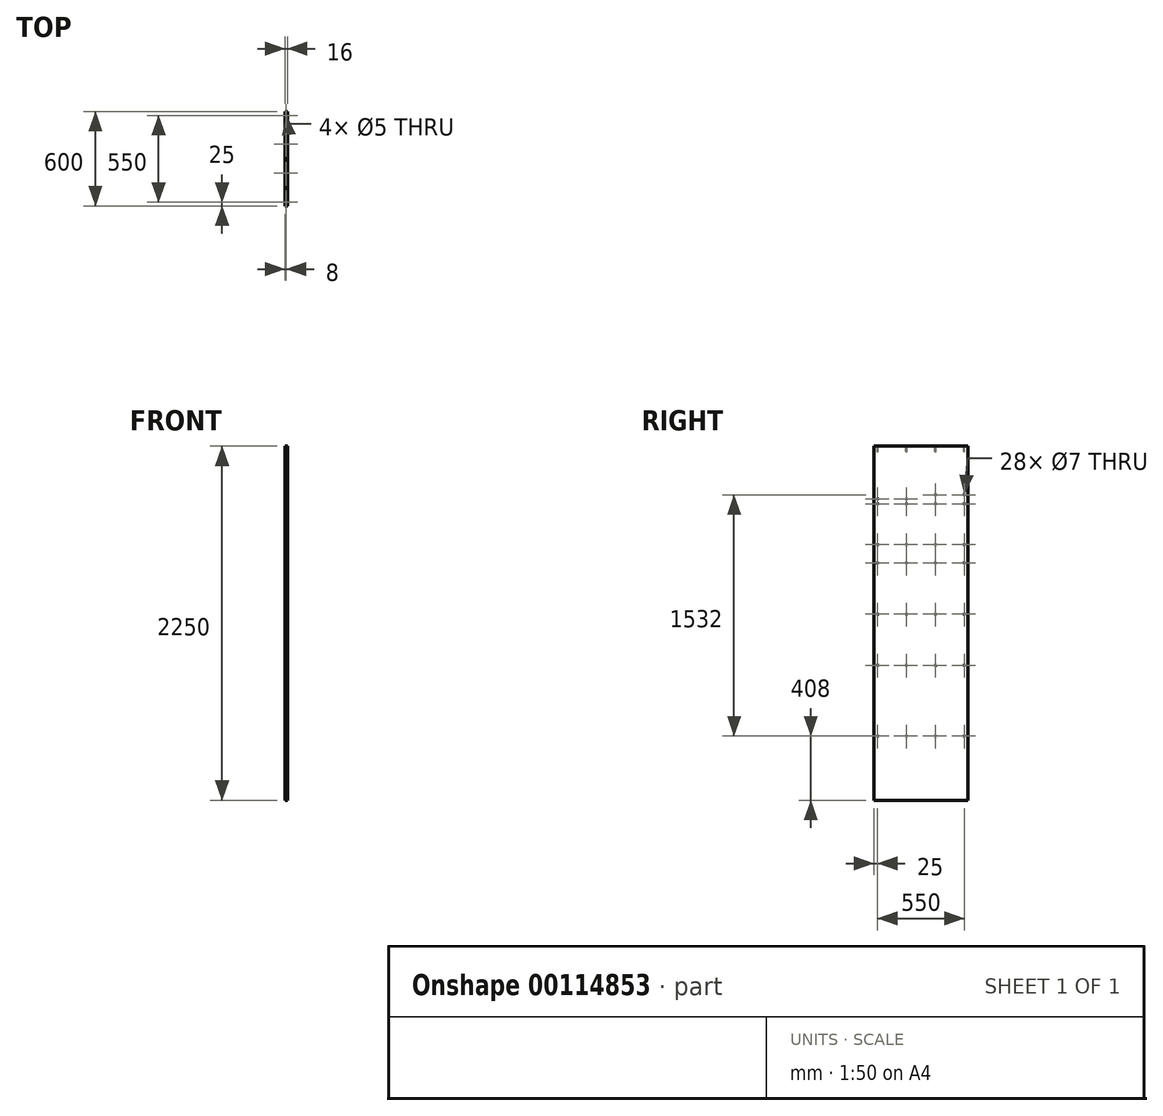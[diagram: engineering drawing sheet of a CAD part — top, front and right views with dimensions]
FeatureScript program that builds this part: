
annotation { "Feature Type Name" : "Feature", "Feature Type Description" : "" }
export const myFeature = defineFeature(function(context is Context, id is Id, definition is map)
    precondition{}
    {
        {
            var Q0;
            Q0=qCreatedBy(makeId("Right.planeOp"),FACE);
            var sketch = newSketch(context, id + "F0", { "sketchPlane" : qUnion([Q0])});
            skLineSegment(sketch, "E0.bottom", {"start": v(-300, 1125) * mm, "end": v(300, 1125) * mm});
            skLineSegment(sketch, "E0.top", {"start": v(-300, -1125) * mm, "end": v(300, -1125) * mm});
            skLineSegment(sketch, "E0.left", {"start": v(-300, 1125) * mm, "end": v(-300, -1125) * mm});
            skLineSegment(sketch, "E0.right", {"start": v(300, 1125) * mm, "end": v(300, -1125) * mm});
            skPoint(sketch, "E0.middle", {"position": v(0, 0) * mm});
            skSolve(sketch);
        }
        {
            var Q0;
            Q0=makeQuery(id+"F0.imprint","IMPRINT",FACE,{"disambiguationData":[TD([[makeQuery(id+"F0.imprint","IMPRINT",EDGE,{"derivedFrom":sQuery(id+"F0.wireOp",EDGE,"E0.bottom")}),-1.0]])]});
            extrude(context, id + "F1", {"entities" : qUnion([Q0]), "endBound" : BoundingType.SYMMETRIC, "depth" : 16 * mm});
        }
        {
            var Q0;
            Q0=makeQuery(id+"F1.opExtrude","SWEPT_FACE",FACE,{"disambiguationData":[OSD([sQuery(id+"F0.wireOp",EDGE,"E0.bottom")])]});
            var sketch = newSketch(context, id + "F2", { "sketchPlane" : qUnion([Q0])});
            skPoint(sketch, "E1", {"position": v(0, 622.7) * mm});
            skPoint(sketch, "E2", {"position": v(0, -275) * mm});
            skPoint(sketch, "E3", {"position": v(0, -92) * mm});
            skPoint(sketch, "E4", {"position": v(0, 275) * mm});
            skPoint(sketch, "E5", {"position": v(0, 92) * mm});
            skSolve(sketch);
        }
        {
            var Q0;
            Q0=sQuery(id+"F2.wireOp",VERTEX,"E4");
            var Q1;
            Q1=sQuery(id+"F2.wireOp",VERTEX,"E5");
            var Q2;
            Q2=sQuery(id+"F2.wireOp",VERTEX,"E3");
            var Q3;
            Q3=sQuery(id+"F2.wireOp",VERTEX,"E2");
            var Q4;
            Q4=makeQuery(id+"F1.opExtrude","SWEPT_BODY",BODY,{"disambiguationData":[OSD([sQuery(id+"F0.wireOp",EDGE,"E0.bottom"),sQuery(id+"F0.wireOp",EDGE,"E0.top"),sQuery(id+"F0.wireOp",EDGE,"E0.left"),sQuery(id+"F0.wireOp",EDGE,"E0.right")])]});
            hole(context, id + "F3", {"style" : HoleStyle.C_SINK, "endStyle" : HoleEndStyle.BLIND, "holeDiameter" : 5 * mm, "cSinkDiameter" : 7 * mm, "cSinkAngle" : 90 * degree, "holeDepth" : 35 * mm, "locations" : qUnion([Q0, Q1, Q2, Q3]), "scope" : qUnion([Q4])});
        }
        {
            var Q0;
            Q0=makeQuery(id+"F1.opExtrude","CAP_FACE",FACE,{"disambiguationData":[OSD([sQuery(id+"F0.wireOp",EDGE,"E0.bottom"),sQuery(id+"F0.wireOp",EDGE,"E0.top"),sQuery(id+"F0.wireOp",EDGE,"E0.left"),sQuery(id+"F0.wireOp",EDGE,"E0.right")])],"isStart":true});
            var sketch = newSketch(context, id + "F4", { "sketchPlane" : qUnion([Q0])});
            skPoint(sketch, "E6", {"position": v(-275, 815) * mm});
            skPoint(sketch, "E7", {"position": v(-92, 815) * mm});
            skPoint(sketch, "E8", {"position": v(275, 790) * mm});
            skPoint(sketch, "E9", {"position": v(92, 790) * mm});
            skPoint(sketch, "E10", {"position": v(-275, 499) * mm});
            skPoint(sketch, "E11", {"position": v(-92, 499) * mm});
            skPoint(sketch, "E12", {"position": v(92, 499) * mm});
            skPoint(sketch, "E13", {"position": v(275, 499) * mm});
            skPoint(sketch, "E14", {"position": v(-275, 758) * mm});
            skPoint(sketch, "E15", {"position": v(-92, 758) * mm});
            skPoint(sketch, "E16", {"position": v(92, 758) * mm});
            skPoint(sketch, "E17", {"position": v(275, 758) * mm});
            skPoint(sketch, "E18", {"position": v(-275, 383) * mm});
            skPoint(sketch, "E19", {"position": v(-92, 383) * mm});
            skPoint(sketch, "E20", {"position": v(92, 383) * mm});
            skPoint(sketch, "E21", {"position": v(275, 383) * mm});
            skPoint(sketch, "E22", {"position": v(-275, 58) * mm});
            skPoint(sketch, "E23", {"position": v(-92, 58) * mm});
            skPoint(sketch, "E24", {"position": v(92, 58) * mm});
            skPoint(sketch, "E25", {"position": v(275, 58) * mm});
            skPoint(sketch, "E26", {"position": v(-275, -267) * mm});
            skPoint(sketch, "E27", {"position": v(-92, -267) * mm});
            skPoint(sketch, "E28", {"position": v(92, -267) * mm});
            skPoint(sketch, "E29", {"position": v(275, -267) * mm});
            skPoint(sketch, "E30", {"position": v(-275, -717) * mm});
            skPoint(sketch, "E31", {"position": v(-92, -717) * mm});
            skPoint(sketch, "E32", {"position": v(92, -717) * mm});
            skPoint(sketch, "E33", {"position": v(275, -717) * mm});
            skSolve(sketch);
        }
        {
            var Q0;
            Q0=sQuery(id+"F4.wireOp",VERTEX,"E6");
            var Q1;
            Q1=sQuery(id+"F4.wireOp",VERTEX,"E7");
            var Q2;
            Q2=sQuery(id+"F4.wireOp",VERTEX,"E9");
            var Q3;
            Q3=sQuery(id+"F4.wireOp",VERTEX,"E8");
            var Q4;
            Q4=sQuery(id+"F4.wireOp",VERTEX,"E17");
            var Q5;
            Q5=sQuery(id+"F4.wireOp",VERTEX,"E16");
            var Q6;
            Q6=sQuery(id+"F4.wireOp",VERTEX,"E15");
            var Q7;
            Q7=sQuery(id+"F4.wireOp",VERTEX,"E14");
            var Q8;
            Q8=sQuery(id+"F4.wireOp",VERTEX,"E10");
            var Q9;
            Q9=sQuery(id+"F4.wireOp",VERTEX,"E11");
            var Q10;
            Q10=sQuery(id+"F4.wireOp",VERTEX,"E12");
            var Q11;
            Q11=sQuery(id+"F4.wireOp",VERTEX,"E13");
            var Q12;
            Q12=sQuery(id+"F4.wireOp",VERTEX,"E21");
            var Q13;
            Q13=sQuery(id+"F4.wireOp",VERTEX,"E20");
            var Q14;
            Q14=sQuery(id+"F4.wireOp",VERTEX,"E19");
            var Q15;
            Q15=sQuery(id+"F4.wireOp",VERTEX,"E18");
            var Q16;
            Q16=sQuery(id+"F4.wireOp",VERTEX,"E22");
            var Q17;
            Q17=sQuery(id+"F4.wireOp",VERTEX,"E23");
            var Q18;
            Q18=sQuery(id+"F4.wireOp",VERTEX,"E24");
            var Q19;
            Q19=sQuery(id+"F4.wireOp",VERTEX,"E25");
            var Q20;
            Q20=sQuery(id+"F4.wireOp",VERTEX,"E29");
            var Q21;
            Q21=sQuery(id+"F4.wireOp",VERTEX,"E28");
            var Q22;
            Q22=sQuery(id+"F4.wireOp",VERTEX,"E27");
            var Q23;
            Q23=sQuery(id+"F4.wireOp",VERTEX,"E26");
            var Q24;
            Q24=sQuery(id+"F4.wireOp",VERTEX,"E30");
            var Q25;
            Q25=sQuery(id+"F4.wireOp",VERTEX,"E31");
            var Q26;
            Q26=sQuery(id+"F4.wireOp",VERTEX,"E32");
            var Q27;
            Q27=sQuery(id+"F4.wireOp",VERTEX,"E33");
            var Q28;
            Q28=makeQuery(id+"F1.opExtrude","SWEPT_BODY",BODY,{"disambiguationData":[OSD([sQuery(id+"F0.wireOp",EDGE,"E0.bottom"),sQuery(id+"F0.wireOp",EDGE,"E0.top"),sQuery(id+"F0.wireOp",EDGE,"E0.left"),sQuery(id+"F0.wireOp",EDGE,"E0.right")])]});
            hole(context, id + "F5", {"style" : HoleStyle.SIMPLE, "endStyle" : HoleEndStyle.THROUGH, "holeDiameter" : 7 * mm, "locations" : qUnion([Q0, Q1, Q2, Q3, Q4, Q5, Q6, Q7, Q8, Q9, Q10, Q11, Q12, Q13, Q14, Q15, Q16, Q17, Q18, Q19, Q20, Q21, Q22, Q23, Q24, Q25, Q26, Q27]), "scope" : qUnion([Q28]), "isTappedThrough" : true});
        }
    });
